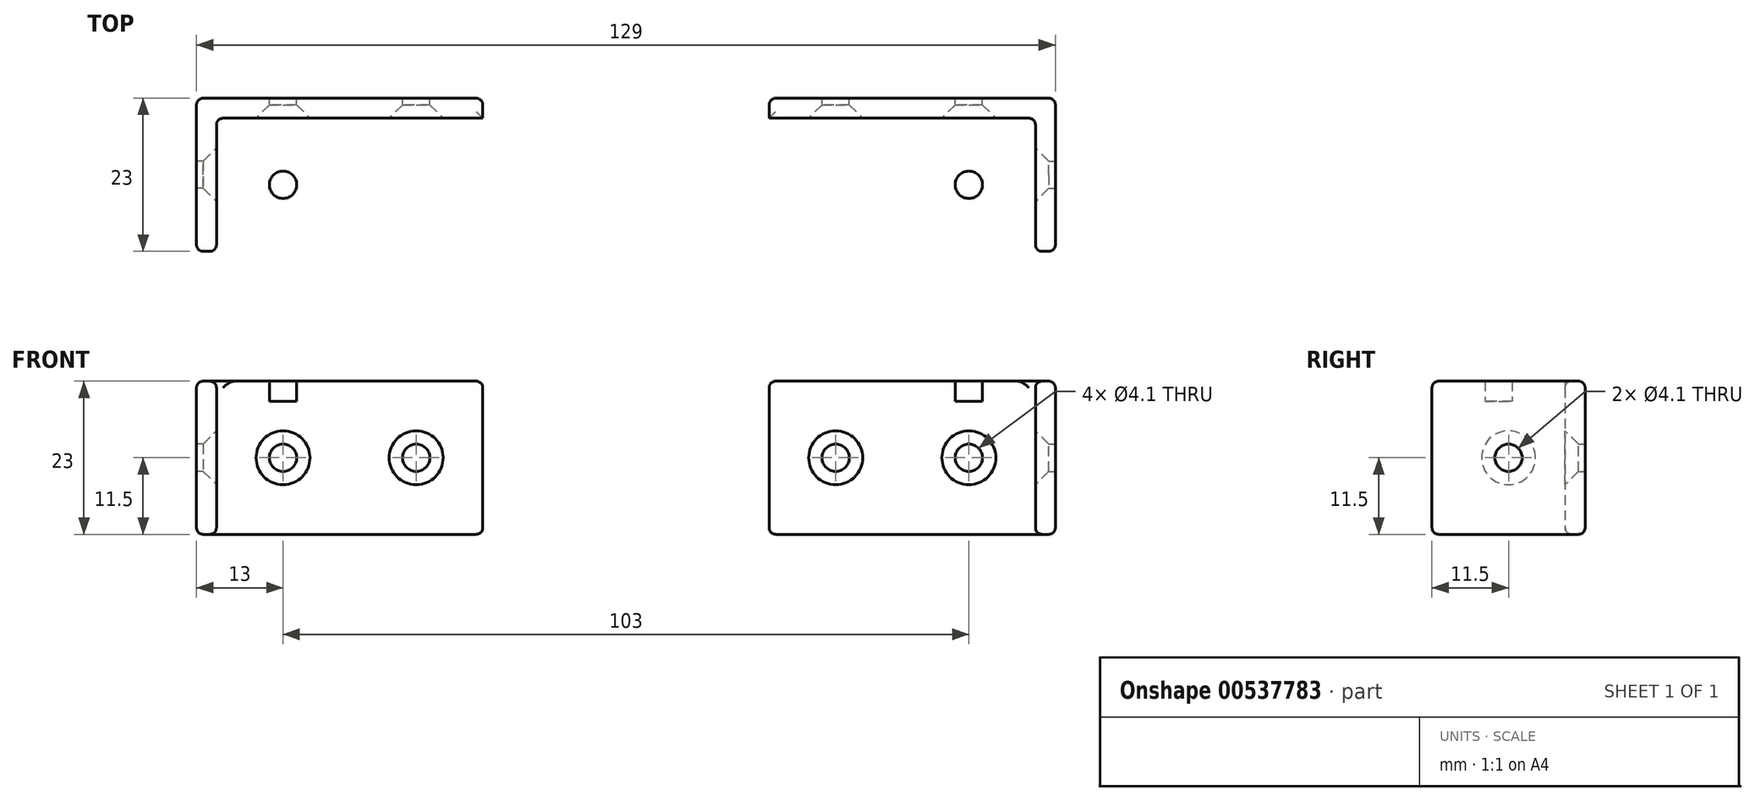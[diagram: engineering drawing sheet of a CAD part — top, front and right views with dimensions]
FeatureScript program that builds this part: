
annotation { "Feature Type Name" : "Feature", "Feature Type Description" : "" }
export const myFeature = defineFeature(function(context is Context, id is Id, definition is map)
    precondition{}
    {
        {
            var Q0;
            Q0=qCreatedBy(makeId("Front.planeOp"),FACE);
            var sketch = newSketch(context, id + "F0", { "sketchPlane" : qUnion([Q0])});
            skLineSegment(sketch, "E0.rect.bottom", {"start": v(21.5, 11.5) * mm, "end": v(-21.5, 11.5) * mm});
            skLineSegment(sketch, "E0.rect.top", {"start": v(21.5, -11.5) * mm, "end": v(-21.5, -11.5) * mm});
            skLineSegment(sketch, "E0.rect.left", {"start": v(21.5, 11.5) * mm, "end": v(21.5, -11.5) * mm});
            skLineSegment(sketch, "E0.rect.right", {"start": v(-21.5, 11.5) * mm, "end": v(-21.5, -11.5) * mm});
            skPoint(sketch, "E0.rect.middle", {"position": v(0, 0) * mm});
            skCircle(sketch, "E1", {"center": v(-11.5, 0) * mm, "radius": 2.05 * mm});
            skCircle(sketch, "E2", {"center": v(8.5, 0) * mm, "radius": 2.05 * mm});
            skSolve(sketch);
        }
        {
            var Q0;
            {var subQ2=sQuery(id+"F0.wireOp",EDGE,"E0.rect.left");Q0=makeQuery(id+"F0.imprint","IMPRINT",FACE,{"disambiguationData":[TD([[makeQuery(id+"F0.imprint","IMPRINT",EDGE,{"derivedFrom":subQ2}),-1.0]])]});}
            extrude(context, id + "F1", {"entities" : qUnion([Q0]), "endBound" : BoundingType.SYMMETRIC, "depth" : 3 * mm});
        }
        {
            var Q0;
            Q0=makeQuery(id+"F1.opExtrude","CAP_FACE",FACE,{"disambiguationData":[OSD([sQuery(id+"F0.wireOp",EDGE,"E0.rect.bottom"),sQuery(id+"F0.wireOp",EDGE,"E0.rect.top"),sQuery(id+"F0.wireOp",EDGE,"E0.rect.left"),sQuery(id+"F0.wireOp",EDGE,"E0.rect.right"),sQuery(id+"F0.wireOp",EDGE,"E1"),sQuery(id+"F0.wireOp",EDGE,"E2")])],"isStart":false});
            var sketch = newSketch(context, id + "F2", { "sketchPlane" : qUnion([Q0])});
            skLineSegment(sketch, "E3.0", {"start": v(21.5, 11.5) * mm, "end": v(-21.5, 11.5) * mm});
            skLineSegment(sketch, "E4.0", {"start": v(21.5, 11.5) * mm, "end": v(21.5, -11.5) * mm});
            skLineSegment(sketch, "E5.0", {"start": v(18.5, 8.5) * mm, "end": v(-21.5, 8.5) * mm});
            skLineSegment(sketch, "E5.1", {"start": v(18.5, 8.5) * mm, "end": v(18.5, -11.5) * mm});
            skLineSegment(sketch, "E6.0", {"start": v(-21.5, 11.5) * mm, "end": v(-21.5, -11.5) * mm});
            skSolve(sketch);
        }
        {
            var Q0;
            {var subQ2=sQuery(id+"F2.wireOp",EDGE,"E3.0");Q0=makeQuery(id+"F2.imprint","IMPRINT",FACE,{"disambiguationData":[TD([[makeQuery(id+"F2.imprint","IMPRINT",EDGE,{"derivedFrom":subQ2}),1.0]])]});}
            extrude(context, id + "F3", {"entities" : qUnion([Q0]), "operationType" : NewBodyOperationType.ADD, "depth" : 20 * mm});
        }
        {
            var Q0;
            Q0=makeQuery(id+"F3.opExtrude","SWEPT_FACE",FACE,{"disambiguationData":[OSD([sQuery(id+"F2.wireOp",EDGE,"E5.0")])]});
            var sketch = newSketch(context, id + "F4", { "sketchPlane" : qUnion([Q0])});
            skLineSegment(sketch, "E7", {"start": v(6.45, -1.5) * mm, "end": v(6.45, 1.5) * mm});
            skLineSegment(sketch, "E8", {"start": v(10.55, 1.5) * mm, "end": v(10.55, -1.5) * mm});
            skLineSegment(sketch, "E9", {"start": v(6.45, 1.5) * mm, "end": v(10.55, 21.5) * mm});
            skCircle(sketch, "E10", {"center": v(8.5, 11.5) * mm, "radius": 2.05 * mm});
            skCircle(sketch, "E11", {"center": v(9.52, -11.2) * mm, "radius": 2.6 * mm});
            skSolve(sketch);
        }
        {
            var Q0;
            {var subQ0=sQuery(id+"F4.wireOp",EDGE,"E10");var subQ1=sQuery(id+"F4.wireOp",EDGE,"E9");var subQ3=makeQuery(id+"F4.imprint","INTERSECT",VERTEX,{"disambiguationData":[OD(0.0)],"derivedFrom":[subQ1,subQ0]});Q0=makeQuery(id+"F4.imprint","IMPRINT",FACE,{"disambiguationData":[TD([[makeQuery(id+"F4.imprint","IMPRINT",EDGE,{"disambiguationData":[TD([[subQ3,-1.0]])],"derivedFrom":subQ1}),1.0]])]});}
            var Q1;
            {var subQ0=sQuery(id+"F4.wireOp",EDGE,"E10");var subQ1=sQuery(id+"F4.wireOp",EDGE,"E9");var subQ3=makeQuery(id+"F4.imprint","INTERSECT",VERTEX,{"disambiguationData":[OD(0.0)],"derivedFrom":[subQ1,subQ0]});Q1=makeQuery(id+"F4.imprint","IMPRINT",FACE,{"disambiguationData":[TD([[makeQuery(id+"F4.imprint","IMPRINT",EDGE,{"disambiguationData":[TD([[subQ3,-1.0]])],"derivedFrom":subQ1}),-1.0]])]});}
            extrude(context, id + "F5", {"entities" : qUnion([Q0, Q1]), "operationType" : NewBodyOperationType.REMOVE, "endBound" : BoundingType.THROUGH_ALL, "oppositeDirection" : true, "depth" : 25.4 * mm});
        }
        {
            var Q0;
            Q0=makeQuery(id+"F3.opExtrude","SWEPT_FACE",FACE,{"disambiguationData":[OSD([sQuery(id+"F2.wireOp",EDGE,"E5.0")])]});
            var sketch = newSketch(context, id + "F6", { "sketchPlane" : qUnion([Q0])});
            skLineSegment(sketch, "E12.0", {"start": v(18.5, 21.5) * mm, "end": v(-21.5, 21.5) * mm});
            skLineSegment(sketch, "E13.0", {"start": v(-21.5, 21.5) * mm, "end": v(-21.5, 1.5) * mm});
            skLineSegment(sketch, "E14", {"start": v(-21.5, 3.5) * mm, "end": v(3.5, 21.5) * mm});
            skSolve(sketch);
        }
        {
            var Q0;
            {var subQ0=sQuery(id+"F6.wireOp",EDGE,"E14");Q0=makeQuery(id+"F6.imprint","IMPRINT",FACE,{"disambiguationData":[TD([[makeQuery(id+"F6.imprint","IMPRINT",EDGE,{"derivedFrom":subQ0}),1.0]])]});}
            extrude(context, id + "F7", {"entities" : qUnion([Q0]), "operationType" : NewBodyOperationType.REMOVE, "endBound" : BoundingType.THROUGH_ALL, "oppositeDirection" : true, "depth" : 25.4 * mm});
        }
        {
            var Q0;
            Q0=makeQuery(id+"F3.boolean.opBoolean","MERGE",FACE,{"derivedFrom":[makeQuery(id+"F1.opExtrude","SWEPT_FACE",FACE,{"disambiguationData":[OSD([sQuery(id+"F0.wireOp",EDGE,"E0.rect.left")])]}),makeQuery(id+"F3.opExtrude","SWEPT_FACE",FACE,{"disambiguationData":[OSD([sQuery(id+"F2.wireOp",EDGE,"E4.0")])]})]});
            var Q1;
            Q1=makeQuery(id+"F1.opExtrude","CAP_EDGE",EDGE,{"disambiguationData":[OSD([sQuery(id+"F0.wireOp",EDGE,"E0.rect.top")])],"isStart":true});
            var Q2;
            Q2=makeQuery(id+"F1.opExtrude","CAP_EDGE",EDGE,{"disambiguationData":[OSD([sQuery(id+"F0.wireOp",EDGE,"E0.rect.bottom")])],"isStart":true});
            var Q3;
            Q3=makeQuery(id+"F3.boolean.opBoolean","MERGE",EDGE,{"derivedFrom":[makeQuery(id+"F1.opExtrude","SWEPT_EDGE",EDGE,{"disambiguationData":[OSD([sQuery(id+"F0.wireOp",EDGE,"E0.rect.bottom"),sQuery(id+"F0.wireOp",EDGE,"E0.rect.right")])]}),makeQuery(id+"F3.opExtrude","SWEPT_EDGE",EDGE,{"disambiguationData":[OSD([sQuery(id+"F2.wireOp",EDGE,"E3.0"),sQuery(id+"F2.wireOp",EDGE,"E6.0")])]})]});
            var Q4;
            Q4=makeQuery(id+"F7.boolean.opBoolean","INTERSECT",EDGE,{"derivedFrom":[makeQuery(id+"F3.boolean.opBoolean","MERGE",FACE,{"derivedFrom":[makeQuery(id+"F1.opExtrude","SWEPT_FACE",FACE,{"disambiguationData":[OSD([sQuery(id+"F0.wireOp",EDGE,"E0.rect.bottom")])]}),makeQuery(id+"F3.opExtrude","SWEPT_FACE",FACE,{"disambiguationData":[OSD([sQuery(id+"F2.wireOp",EDGE,"E3.0")])]})]}),makeQuery(id+"F7.opExtrude","SWEPT_FACE",FACE,{"disambiguationData":[OSD([sQuery(id+"F6.wireOp",EDGE,"E14")])]})]});
            var Q5;
            Q5=makeQuery(id+"F3.opExtrude","CAP_EDGE",EDGE,{"disambiguationData":[OSD([sQuery(id+"F2.wireOp",EDGE,"E3.0")])],"isStart":false});
            var Q6;
            Q6=makeQuery(id+"F7.boolean.opBoolean","COPY",EDGE,{"derivedFrom":makeQuery(id+"F7.opExtrude","CAP_EDGE",EDGE,{"disambiguationData":[OSD([sQuery(id+"F6.wireOp",EDGE,"E14")])],"isStart":true})});
            var Q7;
            Q7=makeQuery(id+"F7.boolean.opBoolean","COPY",EDGE,{"derivedFrom":makeQuery(id+"F7.opExtrude","SWEPT_EDGE",EDGE,{"disambiguationData":[OSD([sQuery(id+"F6.wireOp",EDGE,"E12.0"),sQuery(id+"F6.wireOp",EDGE,"E14")])]})});
            var Q8;
            Q8=makeQuery(id+"F3.opExtrude","CAP_EDGE",EDGE,{"disambiguationData":[OSD([sQuery(id+"F2.wireOp",EDGE,"E5.0")])],"isStart":false});
            var Q9;
            Q9=makeQuery(id+"F3.opExtrude","CAP_EDGE",EDGE,{"disambiguationData":[OSD([sQuery(id+"F2.wireOp",EDGE,"E5.1")])],"isStart":false});
            var Q10;
            Q10=makeQuery(id+"F1.opExtrude","CAP_EDGE",EDGE,{"disambiguationData":[OSD([sQuery(id+"F0.wireOp",EDGE,"E0.rect.top")])],"isStart":false});
            var Q11;
            Q11=makeQuery(id+"F3.opExtrude","SWEPT_FACE",FACE,{"disambiguationData":[OSD([sQuery(id+"F2.wireOp",EDGE,"E5.1")])]});
            var Q12;
            {var subQ0=sQuery(id+"F0.wireOp",EDGE,"E0.rect.top");Q12=makeQuery(id+"F3.boolean.opBoolean","MERGE",FACE,{"derivedFrom":[makeQuery(id+"F1.opExtrude","SWEPT_FACE",FACE,{"disambiguationData":[OSD([subQ0])]}),makeQuery(id+"F3.opExtrude","SWEPT_FACE",FACE,{"disambiguationData":[OSD([subQ0])]})]});}
            var Q13;
            Q13=makeQuery(id+"F1.opExtrude","CAP_EDGE",EDGE,{"disambiguationData":[OSD([sQuery(id+"F0.wireOp",EDGE,"E0.rect.right")])],"isStart":true});
            var Q14;
            Q14=makeQuery(id+"F1.opExtrude","CAP_EDGE",EDGE,{"disambiguationData":[OSD([sQuery(id+"F0.wireOp",EDGE,"E0.rect.right")])],"isStart":false});
            var Q15;
            Q15=makeQuery(id+"F3.opExtrude","SWEPT_EDGE",EDGE,{"disambiguationData":[OSD([sQuery(id+"F2.wireOp",EDGE,"E5.0"),sQuery(id+"F2.wireOp",EDGE,"E6.0")])]});
            var Q16;
            Q16=makeQuery(id+"F7.boolean.opBoolean","COPY",EDGE,{"derivedFrom":makeQuery(id+"F7.opExtrude","SWEPT_EDGE",EDGE,{"disambiguationData":[OSD([sQuery(id+"F6.wireOp",EDGE,"E13.0"),sQuery(id+"F6.wireOp",EDGE,"E14")])]})});
            var Q17;
            Q17=makeQuery(id+"F3.opExtrude","CAP_EDGE",EDGE,{"disambiguationData":[OSD([sQuery(id+"F2.wireOp",EDGE,"E5.0")])],"isStart":true});
            fillet(context, id + "F8", {"entities" : qUnion([Q0, Q1, Q2, Q3, Q4, Q5, Q6, Q7, Q8, Q9, Q10, Q11, Q12, Q13, Q14, Q15, Q16, Q17]), "radius" : 1 * mm, "allowEdgeOverflow" : false});
        }
        {
            var Q0;
            Q0=makeQuery(id+"F1.opExtrude","SWEPT_BODY",BODY,{"disambiguationData":[OSD([sQuery(id+"F0.wireOp",EDGE,"E0.rect.bottom"),sQuery(id+"F0.wireOp",EDGE,"E0.rect.top"),sQuery(id+"F0.wireOp",EDGE,"E0.rect.left"),sQuery(id+"F0.wireOp",EDGE,"E0.rect.right"),sQuery(id+"F0.wireOp",EDGE,"E1"),sQuery(id+"F0.wireOp",EDGE,"E2")])]});
            var Q1;
            Q1=makeQuery(id+"F3.boolean.opBoolean","MERGE",FACE,{"derivedFrom":[makeQuery(id+"F1.opExtrude","SWEPT_FACE",FACE,{"disambiguationData":[OSD([sQuery(id+"F0.wireOp",EDGE,"E0.rect.right")])]}),makeQuery(id+"F3.opExtrude","SWEPT_FACE",FACE,{"disambiguationData":[OSD([sQuery(id+"F2.wireOp",EDGE,"E6.0")])]})]});
            mirror(context, id + "F14", {"entities" : qUnion([Q0]), "mirrorPlane" : qUnion([Q1])});
        }
        {
            var Q0;
            Q0=makeQuery(id+"F1.opExtrude","SWEPT_BODY",BODY,{"disambiguationData":[OSD([sQuery(id+"F0.wireOp",EDGE,"E0.rect.bottom"),sQuery(id+"F0.wireOp",EDGE,"E0.rect.top"),sQuery(id+"F0.wireOp",EDGE,"E0.rect.left"),sQuery(id+"F0.wireOp",EDGE,"E0.rect.right"),sQuery(id+"F0.wireOp",EDGE,"E1"),sQuery(id+"F0.wireOp",EDGE,"E2")])]});
            deleteBodies(context, id + "F9", {"entities" : qUnion([Q0])});
        }
        {
            var Q0;
            Q0=makeQuery(id+"F14.opPattern","COPY",FACE,{"derivedFrom":makeQuery(id+"F3.boolean.opBoolean","MERGE",FACE,{"derivedFrom":[makeQuery(id+"F1.opExtrude","SWEPT_FACE",FACE,{"disambiguationData":[OSD([sQuery(id+"F0.wireOp",EDGE,"E0.rect.left")])]}),makeQuery(id+"F3.opExtrude","SWEPT_FACE",FACE,{"disambiguationData":[OSD([sQuery(id+"F2.wireOp",EDGE,"E4.0")])]})]}),"instanceName":"1"});
            var sketch = newSketch(context, id + "F10", { "sketchPlane" : qUnion([Q0])});
            skLineSegment(sketch, "E15", {"start": v(-0.5, 10.5) * mm, "end": v(20.5, -10.5) * mm, "construction": true});
            skLineSegment(sketch, "E16", {"start": v(20.5, -10.5) * mm, "end": v(20.5, 10.5) * mm, "construction": true});
            skLineSegment(sketch, "E17", {"start": v(20.5, 10.5) * mm, "end": v(-0.5, -10.5) * mm, "construction": true});
            skPoint(sketch, "E18", {"position": v(10, 0) * mm});
            skCircle(sketch, "E19", {"center": v(10, 0) * mm, "radius": 2.05 * mm});
            skSolve(sketch);
        }
        {
            var Q0;
            Q0=makeQuery(id+"F10.imprint","IMPRINT",FACE,{"disambiguationData":[TD([[makeQuery(id+"F10.imprint","IMPRINT",EDGE,{"derivedFrom":sQuery(id+"F10.wireOp",EDGE,"E19")}),1.0]])]});
            extrude(context, id + "F11", {"entities" : qUnion([Q0]), "operationType" : NewBodyOperationType.REMOVE, "endBound" : BoundingType.THROUGH_ALL, "oppositeDirection" : true, "depth" : 25 * mm, "offsetDistance" : 25 * mm});
        }
        {
            var Q0;
            Q0=makeQuery(id+"F14.opPattern","COPY",BODY,{"derivedFrom":makeQuery(id+"F1.opExtrude","SWEPT_BODY",BODY,{"disambiguationData":[OSD([sQuery(id+"F0.wireOp",EDGE,"E0.rect.bottom"),sQuery(id+"F0.wireOp",EDGE,"E0.rect.top"),sQuery(id+"F0.wireOp",EDGE,"E0.rect.left"),sQuery(id+"F0.wireOp",EDGE,"E0.rect.right"),sQuery(id+"F0.wireOp",EDGE,"E1"),sQuery(id+"F0.wireOp",EDGE,"E2")])]}),"instanceName":"1"});
            var Q1;
            Q1=qCreatedBy(makeId("Right.planeOp"),FACE);
            mirror(context, id + "F12", {"entities" : qUnion([Q0]), "mirrorPlane" : qUnion([Q1])});
        }
        {
            var Q0;
            Q0=makeQuery(id+"F14.opPattern","COPY",EDGE,{"derivedFrom":makeQuery(id+"F5.boolean.opBoolean","COPY",EDGE,{"derivedFrom":makeQuery(id+"F5.opExtrude","CAP_EDGE",EDGE,{"disambiguationData":[OSD([sQuery(id+"F4.wireOp",EDGE,"E10")])],"isStart":true})}),"instanceName":"1"});
            var Q1;
            Q1=makeQuery(id+"F14.opPattern","COPY",EDGE,{"derivedFrom":makeQuery(id+"F1.opExtrude","CAP_EDGE",EDGE,{"disambiguationData":[OSD([sQuery(id+"F0.wireOp",EDGE,"E2")])],"isStart":false}),"instanceName":"1"});
            var Q2;
            Q2=makeQuery(id+"F14.opPattern","COPY",EDGE,{"derivedFrom":makeQuery(id+"F1.opExtrude","CAP_EDGE",EDGE,{"disambiguationData":[OSD([sQuery(id+"F0.wireOp",EDGE,"E1")])],"isStart":false}),"instanceName":"1"});
            var Q3;
            Q3=makeQuery(id+"F12.opPattern","COPY",EDGE,{"derivedFrom":makeQuery(id+"F14.opPattern","COPY",EDGE,{"derivedFrom":makeQuery(id+"F1.opExtrude","CAP_EDGE",EDGE,{"disambiguationData":[OSD([sQuery(id+"F0.wireOp",EDGE,"E1")])],"isStart":false}),"instanceName":"1"}),"instanceName":"1"});
            var Q4;
            Q4=makeQuery(id+"F12.opPattern","COPY",EDGE,{"derivedFrom":makeQuery(id+"F14.opPattern","COPY",EDGE,{"derivedFrom":makeQuery(id+"F1.opExtrude","CAP_EDGE",EDGE,{"disambiguationData":[OSD([sQuery(id+"F0.wireOp",EDGE,"E2")])],"isStart":false}),"instanceName":"1"}),"instanceName":"1"});
            var Q5;
            Q5=makeQuery(id+"F12.opPattern","COPY",EDGE,{"derivedFrom":makeQuery(id+"F14.opPattern","COPY",EDGE,{"derivedFrom":makeQuery(id+"F5.boolean.opBoolean","COPY",EDGE,{"derivedFrom":makeQuery(id+"F5.opExtrude","CAP_EDGE",EDGE,{"disambiguationData":[OSD([sQuery(id+"F4.wireOp",EDGE,"E10")])],"isStart":true})}),"instanceName":"1"}),"instanceName":"1"});
            var Q6;
            Q6=makeQuery(id+"F11.boolean.opBoolean","INTERSECT",EDGE,{"derivedFrom":[makeQuery(id+"F14.opPattern","COPY",FACE,{"derivedFrom":makeQuery(id+"F3.opExtrude","SWEPT_FACE",FACE,{"disambiguationData":[OSD([sQuery(id+"F2.wireOp",EDGE,"E5.1")])]}),"instanceName":"1"}),makeQuery(id+"F11.opExtrude","SWEPT_FACE",FACE,{"disambiguationData":[OSD([sQuery(id+"F10.wireOp",EDGE,"E19")])]})]});
            var Q7;
            Q7=makeQuery(id+"F12.opPattern","COPY",EDGE,{"derivedFrom":makeQuery(id+"F11.boolean.opBoolean","INTERSECT",EDGE,{"derivedFrom":[makeQuery(id+"F14.opPattern","COPY",FACE,{"derivedFrom":makeQuery(id+"F3.opExtrude","SWEPT_FACE",FACE,{"disambiguationData":[OSD([sQuery(id+"F2.wireOp",EDGE,"E5.1")])]}),"instanceName":"1"}),makeQuery(id+"F11.opExtrude","SWEPT_FACE",FACE,{"disambiguationData":[OSD([sQuery(id+"F10.wireOp",EDGE,"E19")])]})]}),"instanceName":"1"});
            chamfer(context, id + "F13", {"entities" : qUnion([Q0, Q1, Q2, Q3, Q4, Q5, Q6, Q7]), "width" : 2 * mm, "tangentPropagation" : true});
        }
    });
